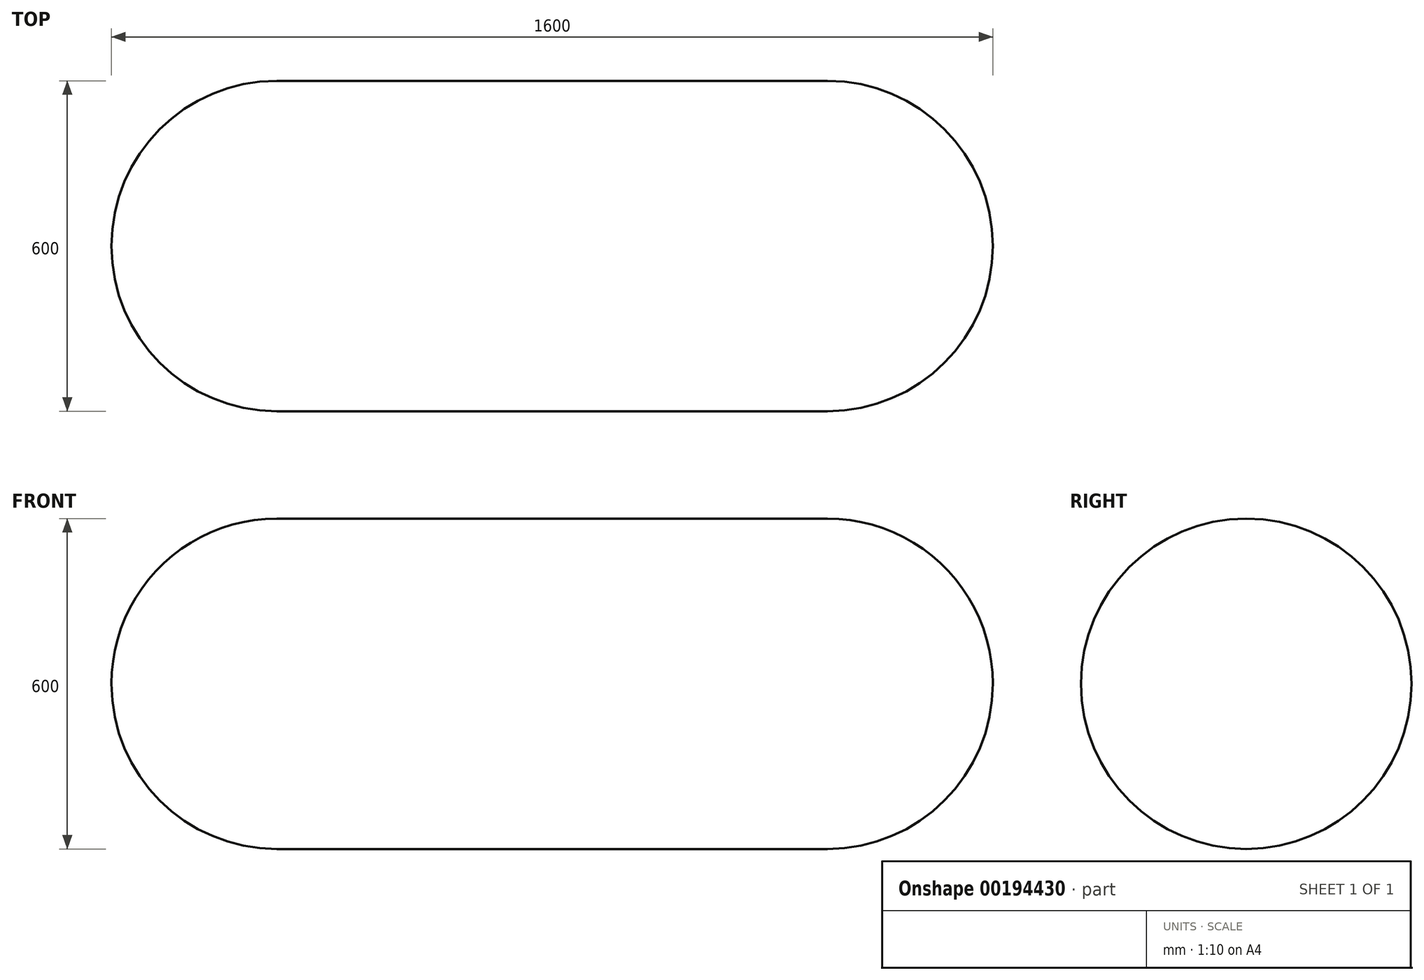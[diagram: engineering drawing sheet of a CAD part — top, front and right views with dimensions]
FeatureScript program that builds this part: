
annotation { "Feature Type Name" : "Feature", "Feature Type Description" : "" }
export const myFeature = defineFeature(function(context is Context, id is Id, definition is map)
    precondition{}
    {
        {
            var Q0;
            Q0=qCreatedBy(makeId("Front.planeOp"),FACE);
            var sketch = newSketch(context, id + "F0", { "sketchPlane" : qUnion([Q0])});
            skLineSegment(sketch, "E0", {"start": v(0, 300) * mm, "end": v(-500, 300) * mm});
            skArc(sketch, "E1", {"start": v(-500, 300) * mm, "mid": v(-712.13, 212.13) * mm, "end": v(-800, 0) * mm});
            skLineSegment(sketch, "E2", {"start": v(-500, 0) * mm, "end": v(-500, 300) * mm, "construction": true});
            skLineSegment(sketch, "E3", {"start": v(-500, 0) * mm, "end": v(-800, 0) * mm, "construction": true});
            skLineSegment(sketch, "E4.MirrorCS", {"start": v(0, 300) * mm, "end": v(500, 300) * mm});
            skArc(sketch, "E5.MirrorCS", {"start": v(500, 300) * mm, "mid": v(712.13, 212.13) * mm, "end": v(800, 0) * mm});
            skLineSegment(sketch, "E6", {"start": v(-800, 0) * mm, "end": v(800, 0) * mm});
            skSolve(sketch);
        }
        {
            var Q0;
            Q0=makeQuery(id+"F0.imprint","IMPRINT",FACE,{"disambiguationData":[TD([[makeQuery(id+"F0.imprint","IMPRINT",EDGE,{"derivedFrom":sQuery(id+"F0.wireOp",EDGE,"E0")}),1.0]])]});
            var Q1;
            Q1=sQuery(id+"F0.wireOp",EDGE,"E6");
            revolve(context, id + "F1", {"entities" : qUnion([Q0]), "axis" : qUnion([Q1]), "revolveType" : RevolveType.FULL});
        }
    });
